# Revit family: Concealed Cistern with 90 degree grabrail
name_source: partatom
category: Plumbing Fixtures
revit_build: Autodesk Revit 2016 (Build: 20160314_0715(x64)
units: mm (PartAtom-declared; Revit-internal decimal feet)

## family parameters
Always vertical = Yes
Cut with Voids When Loaded = No
Part Type = Normal
Room Calculation Point = No
Round Connector Dimension = Use Diameter
Shared = No
Work Plane-Based = No

## types (1)
- RBA4150-101
    Accessible Compliant = AS1428.1-2009 Compliant
    BAR = Stainless Steel, Satin Finish
    BothGrabRails_Vertical_Offset = 810 mm
    BothGrabRails_Vertical_calc = 810 mm
    Description = Accessible Compliant Backrest
    Exclusion zone = Yes
    Manufacturer = RBA Group
    Model = RBA4150-101
    Modified Issue = 20160802.01
    PaperHolder_Horizontal_Offset = 1050 mm  [stored 3.44488 ft]
    PaperHolder_Horizontal_calc = 1050 mm  [stored 3.44488 ft]
    PaperHolder_Vertical_Offset = 650 mm  [stored 2.13255 ft]
    PaperHolder_Vertical_calc = 650 mm  [stored 2.13255 ft]
    SmallGrabRail_Horizontal_Offset = 517 mm  [stored 1.69619 ft]
    SmallGrabRail_Horizontal_calc = 517 mm  [stored 1.69619 ft]

note: [stored X ft] marks values corroborated as IEEE doubles in the binary element streams (Revit-internal decimal feet)

## geometry (parser evidence)
native form markers: Blend x74, Sweep x20
no freeform markers — native parametric forms only
